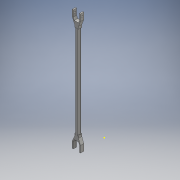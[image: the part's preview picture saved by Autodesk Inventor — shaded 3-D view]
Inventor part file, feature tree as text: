
AUTODESK INVENTOR PART (.ipt)
format: ipt  version: 2016 (Build 200138000, 138)  size: 191,488 bytes
history: native  units: mm
features: sketch x7, extrude x6
ambient origin geometry x8: Origin, YZ Plane, XZ Plane, XY Plane, X Axis, Y Axis, Z Axis, Center Point
bodies: Solid1 (feature_tree)
feature tree (13):
  extrude  "Extrusion1"  Depth=180.0mm TaperAngle=0.0deg
  extrude  "Extrusion2"  Depth=2.0mm
  sketch  "Sketch3"  dims[d16=27.824719mm d17=11.0mm]
  extrude  "Extrusion3"  Depth=11.0mm
  extrude  "Extrusion4"  Depth=6.5mm TaperAngle=0.0deg
  extrude  "Extrusion5"  Depth=6.5mm
  extrude  "Extrusion6"  Depth=6.5mm TaperAngle=0.0deg
  sketch  "Sketch1"  dims[d0=7.5mm d1=180.0mm d2=0.0mm]
  sketch  "Sketch2"  dims[d12=2.0mm d13=2.0mm]
  sketch  "Sketch5"  dims[d21=12.0mm d22=6.5mm d23=0.0mm]
  sketch  "Sketch6"  dims[d25=6.5mm d26=0.0mm d27=6.0mm]
  sketch  "Sketch7"  dims[d28=3.0mm d29=6.5mm d30=0.0mm]
  sketch  "Sketch8"  dims[d31=2.0mm d32=2.0mm d34=2.0mm d35=2.0mm d36=11.0mm d37=12.0mm d38=2.0mm d39=2.0mm d40=6.5mm d41=0.0mm d42=6.5mm d43=0.0mm]
